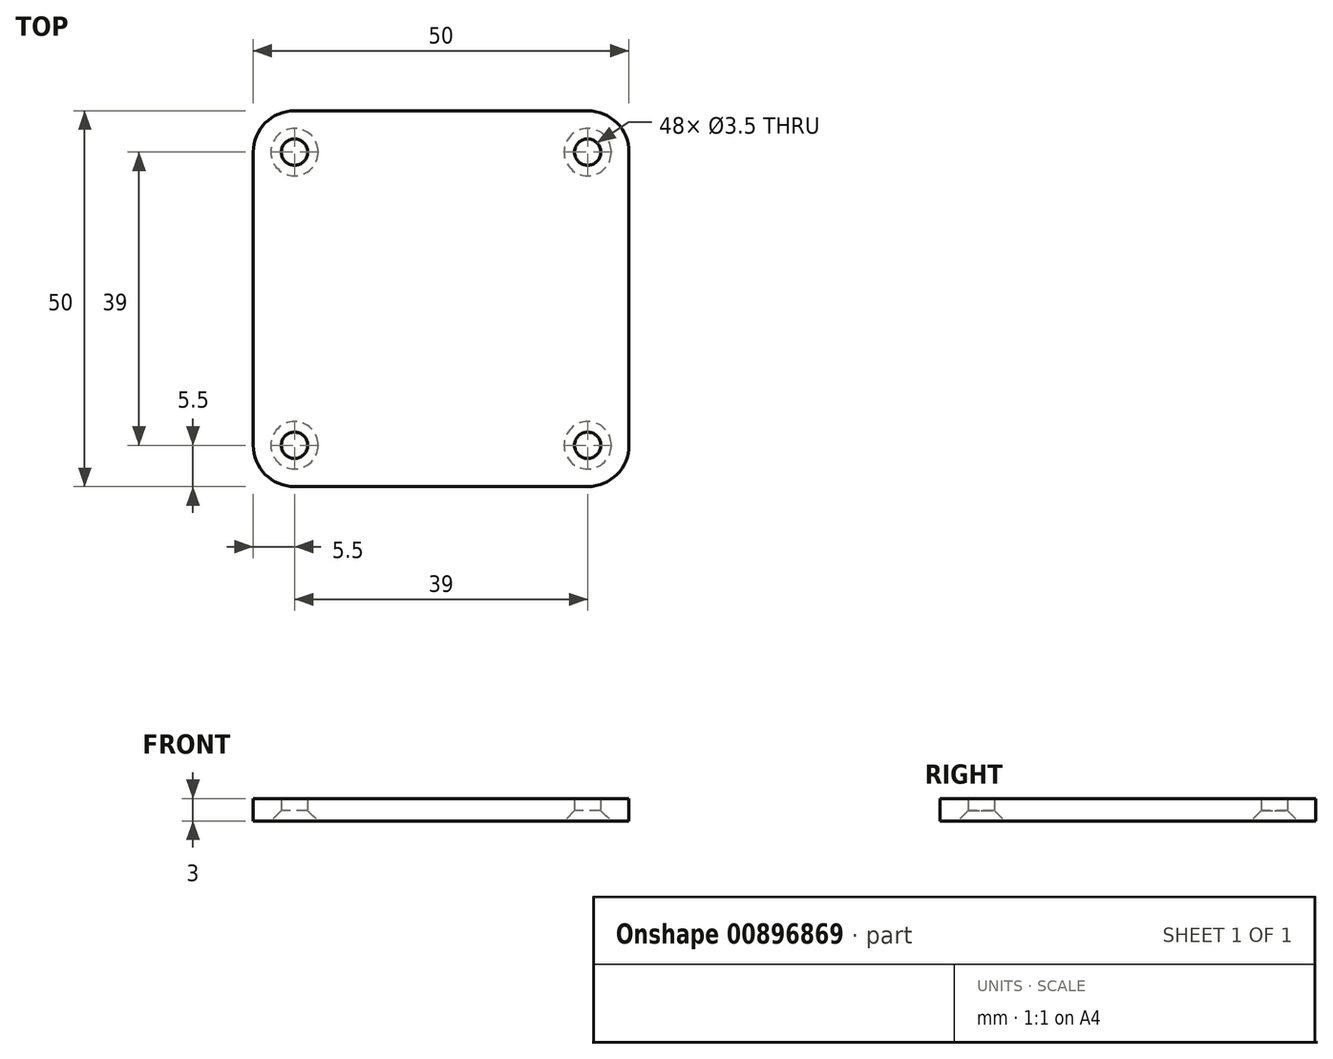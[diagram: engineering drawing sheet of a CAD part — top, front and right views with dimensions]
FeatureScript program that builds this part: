
annotation { "Feature Type Name" : "Feature", "Feature Type Description" : "" }
export const myFeature = defineFeature(function(context is Context, id is Id, definition is map)
    precondition{}
    {
        {
            var Q0;
            Q0=qCreatedBy(makeId("Top.planeOp"),FACE);
            var sketch = newSketch(context, id + "F0", { "sketchPlane" : qUnion([Q0])});
            skLineSegment(sketch, "E0.bottom", {"start": v(-25, -25) * mm, "end": v(25, -25) * mm});
            skLineSegment(sketch, "E0.top", {"start": v(-25, 25) * mm, "end": v(25, 25) * mm});
            skLineSegment(sketch, "E0.left", {"start": v(-25, -25) * mm, "end": v(-25, 25) * mm});
            skLineSegment(sketch, "E0.right", {"start": v(25, -25) * mm, "end": v(25, 25) * mm});
            skCircle(sketch, "E1", {"center": v(-19.5, 19.5) * mm, "radius": 1.75 * mm});
            skCircle(sketch, "E2", {"center": v(19.5, 19.5) * mm, "radius": 1.75 * mm});
            skCircle(sketch, "E3", {"center": v(19.5, -19.5) * mm, "radius": 1.75 * mm});
            skCircle(sketch, "E4", {"center": v(-19.5, -19.5) * mm, "radius": 1.75 * mm});
            skSolve(sketch);
        }
        {
            var Q0;
            Q0 = qSketchRegion(id + "F0", true);
            extrude(context, id + "F1", {"entities" : qUnion([Q0]), "depth" : 3 * mm, "offsetDistance" : 25 * mm});
        }
        {
            var Q0;
            Q0=makeQuery(id+"F1.opExtrude","SWEPT_EDGE",EDGE,{"disambiguationData":[OSD([sQuery(id+"F0.wireOp",EDGE,"E0.bottom"),sQuery(id+"F0.wireOp",EDGE,"E0.left")])]});
            var Q1;
            Q1=makeQuery(id+"F1.opExtrude","SWEPT_EDGE",EDGE,{"disambiguationData":[OSD([sQuery(id+"F0.wireOp",EDGE,"E0.bottom"),sQuery(id+"F0.wireOp",EDGE,"E0.right")])]});
            var Q2;
            Q2=makeQuery(id+"F1.opExtrude","SWEPT_EDGE",EDGE,{"disambiguationData":[OSD([sQuery(id+"F0.wireOp",EDGE,"E0.top"),sQuery(id+"F0.wireOp",EDGE,"E0.right")])]});
            var Q3;
            Q3=makeQuery(id+"F1.opExtrude","SWEPT_EDGE",EDGE,{"disambiguationData":[OSD([sQuery(id+"F0.wireOp",EDGE,"E0.top"),sQuery(id+"F0.wireOp",EDGE,"E0.left")])]});
            fillet(context, id + "F2", {"entities" : qUnion([Q0, Q1, Q2, Q3]), "radius" : 5.5 * mm, "tangentPropagation" : true, "allowEdgeOverflow" : false});
        }
        {
            var Q0;
            Q0=makeQuery(id+"F1.opExtrude","CAP_EDGE",EDGE,{"disambiguationData":[OSD([sQuery(id+"F0.wireOp",EDGE,"E4")])],"isStart":true});
            var Q1;
            Q1=makeQuery(id+"F1.opExtrude","CAP_EDGE",EDGE,{"disambiguationData":[OSD([sQuery(id+"F0.wireOp",EDGE,"E1")])],"isStart":true});
            var Q2;
            Q2=makeQuery(id+"F1.opExtrude","CAP_EDGE",EDGE,{"disambiguationData":[OSD([sQuery(id+"F0.wireOp",EDGE,"E2")])],"isStart":true});
            var Q3;
            Q3=makeQuery(id+"F1.opExtrude","CAP_EDGE",EDGE,{"disambiguationData":[OSD([sQuery(id+"F0.wireOp",EDGE,"E3")])],"isStart":true});
            chamfer(context, id + "F3", {"entities" : qUnion([Q0, Q1, Q2, Q3]), "width" : 1.4 * mm, "tangentPropagation" : true});
        }
    });
